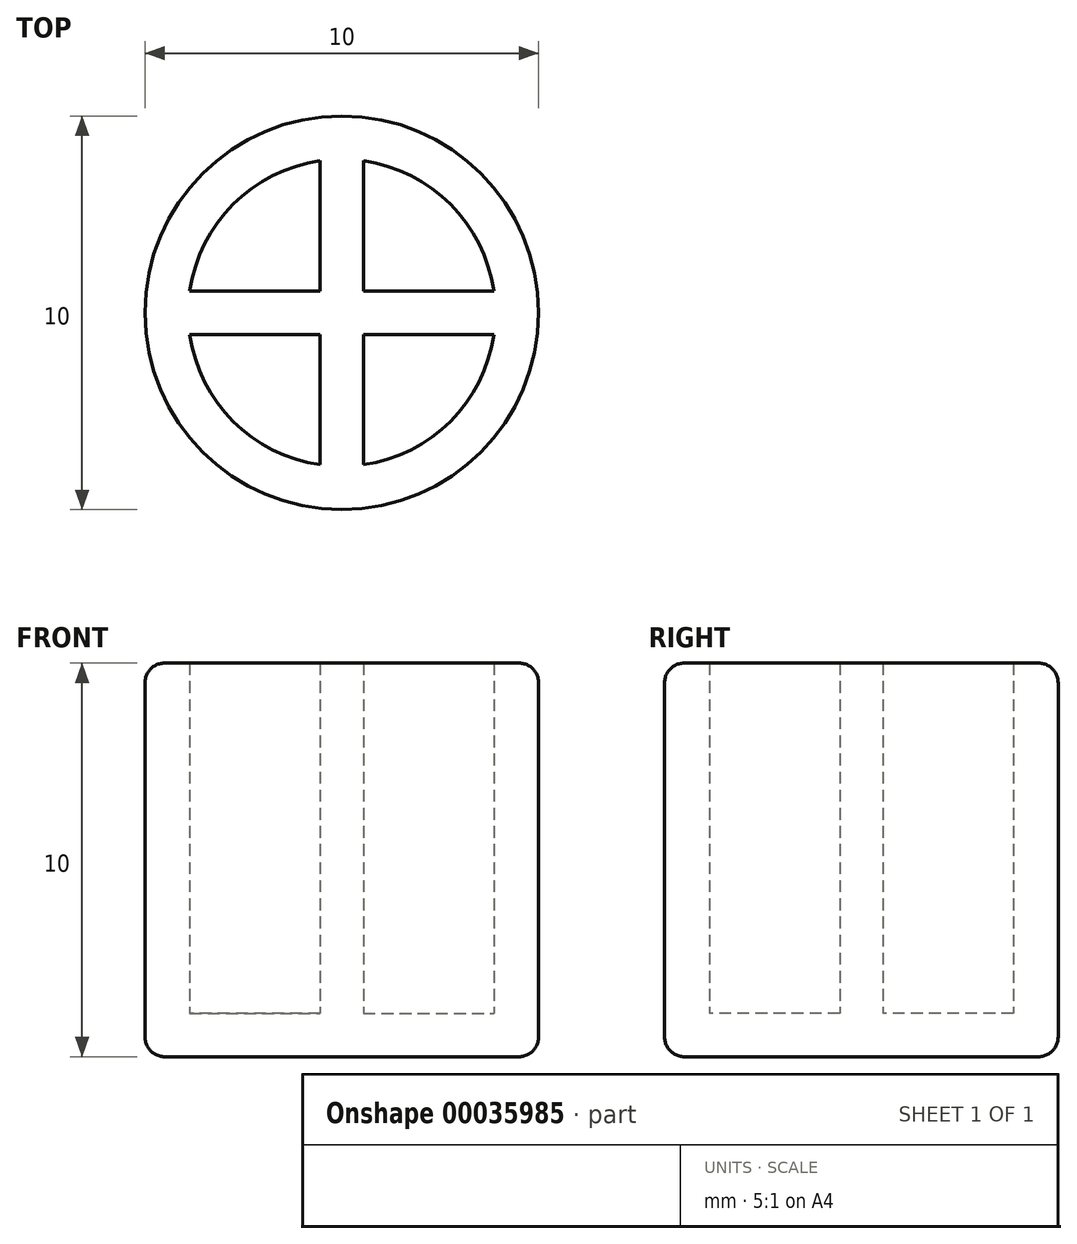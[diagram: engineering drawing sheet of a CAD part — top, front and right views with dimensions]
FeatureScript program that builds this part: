
annotation { "Feature Type Name" : "Feature", "Feature Type Description" : "" }
export const myFeature = defineFeature(function(context is Context, id is Id, definition is map)
    precondition{}
    {
        {
            var Q0;
            Q0=qCreatedBy(makeId("Top.planeOp"),FACE);
            var sketch = newSketch(context, id + "F0", { "sketchPlane" : qUnion([Q0])});
            skCircle(sketch, "E0", {"center": v(0, 0) * mm, "radius": 5 * mm});
            skSolve(sketch);
        }
        {
            var Q0;
            Q0 = qSketchRegion(id + "F0", true);
            extrude(context, id + "F1", {"entities" : qUnion([Q0]), "depth" : 10 * mm});
        }
        {
            var Q0;
            Q0=makeQuery(id+"F1.opExtrude","CAP_FACE",FACE,{"disambiguationData":[OSD([sQuery(id+"F0.wireOp",EDGE,"E0")])],"isStart":false});
            shell(context, id + "F2", {"entities" : qUnion([Q0]), "thickness" : 1.1 * mm});
        }
        {
            var Q0;
            {var subQ0=sQuery(id+"F0.wireOp",EDGE,"E0");Q0=makeQuery(id+"F2.opShell","OFFSET_FACE",FACE,{"disambiguationData":[OSD([subQ0]),TDD([makeQuery(id+"F1.opExtrude","CAP_FACE",FACE,{"disambiguationData":[OSD([subQ0])],"isStart":true})])]});}
            var sketch = newSketch(context, id + "F3", { "sketchPlane" : qUnion([Q0])});
            skLineSegment(sketch, "E1", {"start": v(-3.86, 0.55) * mm, "end": v(-0.55, 0.55) * mm});
            skLineSegment(sketch, "E2", {"start": v(-3.86, -0.55) * mm, "end": v(-0.55, -0.55) * mm});
            skLineSegment(sketch, "E3", {"start": v(-0.55, 3.86) * mm, "end": v(-0.55, 0.55) * mm});
            skLineSegment(sketch, "E4", {"start": v(0.55, 3.86) * mm, "end": v(0.55, 0.55) * mm});
            skLineSegment(sketch, "E5.trimOffspring", {"start": v(0.55, 0.55) * mm, "end": v(3.86, 0.55) * mm});
            skLineSegment(sketch, "E6.trimOffspring", {"start": v(-0.55, -0.55) * mm, "end": v(-0.55, -3.86) * mm});
            skLineSegment(sketch, "E7.trimOffspring", {"start": v(0.55, -0.55) * mm, "end": v(0.55, -3.86) * mm});
            skLineSegment(sketch, "E8.trimOffspring", {"start": v(0.55, -0.55) * mm, "end": v(3.86, -0.55) * mm});
            skArc(sketch, "E9", {"start": v(0.55, 3.86) * mm, "mid": v(0, 3.9) * mm, "end": v(-0.55, 3.86) * mm});
            skArc(sketch, "E10.trimOffspring", {"start": v(3.86, -0.55) * mm, "mid": v(3.9, 0) * mm, "end": v(3.86, 0.55) * mm});
            skArc(sketch, "E11.trimOffspring", {"start": v(-0.55, -3.86) * mm, "mid": v(0, -3.9) * mm, "end": v(0.55, -3.86) * mm});
            skArc(sketch, "E12.trimOffspring", {"start": v(-3.86, 0.55) * mm, "mid": v(-3.9, 0) * mm, "end": v(-3.86, -0.55) * mm});
            skSolve(sketch);
        }
        {
            var Q0;
            Q0 = qSketchRegion(id + "F3", true);
            var Q1;
            Q1=makeQuery(id+"F1.opExtrude","CAP_FACE",FACE,{"disambiguationData":[OSD([sQuery(id+"F0.wireOp",EDGE,"E0")])],"isStart":false});
            extrude(context, id + "F4", {"entities" : qUnion([Q0]), "operationType" : NewBodyOperationType.ADD, "endBound" : BoundingType.UP_TO_SURFACE, "endBoundEntityFace" : qUnion([Q1]), "depth" : 25 * mm});
        }
        {
            var Q0;
            Q0=makeQuery(id+"F1.opExtrude","CAP_EDGE",EDGE,{"disambiguationData":[OSD([sQuery(id+"F0.wireOp",EDGE,"E0")])],"isStart":false});
            var Q1;
            Q1=makeQuery(id+"F1.opExtrude","CAP_EDGE",EDGE,{"disambiguationData":[OSD([sQuery(id+"F0.wireOp",EDGE,"E0")])],"isStart":true});
            fillet(context, id + "F5", {"entities" : qUnion([Q0, Q1]), "radius" : .5 * mm, "tangentPropagation" : true, "allowEdgeOverflow" : false});
        }
    });
